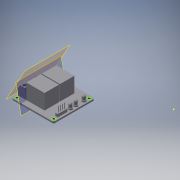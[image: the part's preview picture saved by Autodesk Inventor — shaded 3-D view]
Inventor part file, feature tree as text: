
AUTODESK INVENTOR PART (.ipt)
format: ipt  version: 2016 (Build 200138000, 138)  size: 401,920 bytes
history: native  units: in
note: dims shown in document units (in); Inventor stores cm internally (conversion verified against a paired STEP export)
features: sketch x21, extrude x20, fillet x2, plane x2, chamfer x1
ambient origin geometry x8: Origin, YZ Plane, XZ Plane, XY Plane, X Axis, Y Axis, Z Axis, Center Point
bodies: Solid1 (feature_tree)
feature tree (46):
  extrude  "Extrusion1"  Depth=1.7126in
  extrude  "Extrusion2"  Depth=0.1181in
  sketch  "Sketch3"  dims[d5=0.1181in d6=1.4409in]
  extrude  "Extrusion4"  Depth=1.4409in
  extrude  "Extrusion5"  Depth=0.1142in
  extrude  "Extrusion6"  Depth=0.1181in
  sketch  "Sketch7"  dims[d13=1.4961in d14=0.1024in]
  sketch  "Sketch8"  dims[d15=0.063in d16=0.0in d17=0.5906in d18=0.5906in]
  sketch  "Sketch9"  dims[d19=0.5906in d20=0.5906in]
  extrude  "Extrusion7"  Depth=0.1181in
  extrude  "Extrusion8"  Depth=1.4961in
  extrude  "Extrusion9"  Depth=0.5906in
  fillet  "Fillet1"  Radius=0.5906in
  extrude  "Extrusion10"  Depth=0.5906in
  extrude  "Extrusion11"  Depth=0.2205in
  extrude  "Extrusion12"  Depth=0.3937in
  plane  "Work Plane2"
  extrude  "Extrusion13"  Depth=0.0984in
  plane  "Work Plane3"
  extrude  "Extrusion14"  Depth=0.1181in TaperAngle=0.0deg
  extrude  "Extrusion15"  Depth=0.0236in
  extrude  "Extrusion16"  Depth=0.0236in
  extrude  "Extrusion17"  Depth=0.0512in
  extrude  "Extrusion18"  Depth=0.0827in
  extrude  "Extrusion19"  Depth=0.0512in
  extrude  "Extrusion20"  Depth=0.1575in
  extrude  "Extrusion21"  Depth=0.1575in
  chamfer  "Chamfer1"  Distance=0.3307in
  fillet  "Fillet2"  Radius=0.2165in
  sketch  "Sketch21"  dims[d48=0.315in d49=0.3307in d50=0.2165in d51=0.1299in d52=0.0472in d53=0.0in d54=0.1181in d55=0.1181in d56=0.1181in d57=0.1693in d58=0.0in d59=0.1693in d60=0.0in d61=0.1693in d62=0.0in d63=0.0591in d64=0.315in d65=0.0276in d66=0.2402in d67=0.5906in d68=0.5906in d69=0.0394in d70=0.2362in d71=0.0in d72=0.1693in d73=0.1969in d74=0.0315in d75=0.1693in d76=0.1693in d77=0.1969in d78=0.0236in d79=0.0236in d80=0.0157in d81=0.0394in d82=0.0in d83=0.0in d84=0.0in d85=0.0591in d86=0.1969in d87=0.1575in d88=0.0in d89=0.0787in d90=0.0in d91=0.0787in d92=0.0in d93=0.1417in d94=0.1417in d95=0.1417in d96=0.0984in d97=0.1969in d98=0.1969in d100=0.0787in d101=0.0in d102=0.1969in d103=0.1575in d104=0.0in d105=0.1575in d106=0.0in d107=0.1575in d108=0.0in d109=0.1417in d110=0.1417in d111=0.1417in d112=0.0984in d113=0.0551in d115=0.0551in d116=0.0984in d117=0.0984in d118=0.0984in d119=0.0787in d120=0.0in d121=0.1693in d122=0.1969in d123=0.1693in d124=0.1969in d125=0.1693in d126=0.1969in d127=0.0157in d128=0.0236in d129=0.0236in d130=0.0394in d131=0.0in d132=0.6181in d133=0.0in d134=0.0394in d135=0.0787in d136=45.0deg d137=0.0079in]
  sketch  "Sketch1"  dims[d0=1.6772in d1=1.7126in]
  sketch  "Sketch2"  dims[d2=0.063in d3=0.0in d4=0.1181in]
  sketch  "Sketch4"  dims[d7=0.1142in d8=0.1142in]
  sketch  "Sketch5"  dims[d9=0.1142in d10=0.1181in]
  sketch  "Sketch6"  dims[d11=1.4961in d12=0.1181in]
  sketch  "Sketch10"  dims[d21=0.7402in d22=0.2205in]
  sketch  "Sketch11"  dims[d23=0.0394in d26=0.3937in]
  sketch  "Sketch12"  dims[d27=0.0787in d28=0.0984in]
  sketch  "Sketch13"  dims[d29=0.248in d30=0.1181in d31=0.0in]
  sketch  "Sketch14"  dims[d32=0.0236in d33=0.0236in]
  sketch  "Sketch15"  dims[d34=0.0236in d35=0.0236in]
  sketch  "Sketch16"  dims[d36=0.0728in d37=0.0512in]
  sketch  "Sketch17"  dims[d38=0.0827in d39=0.0827in]
  sketch  "Sketch18"  dims[d40=0.0827in d41=0.0512in]
  sketch  "Sketch19"  dims[d42=0.2283in d43=0.0in d44=0.1575in]
  sketch  "Sketch20"  dims[d45=0.1575in d46=0.1575in]
